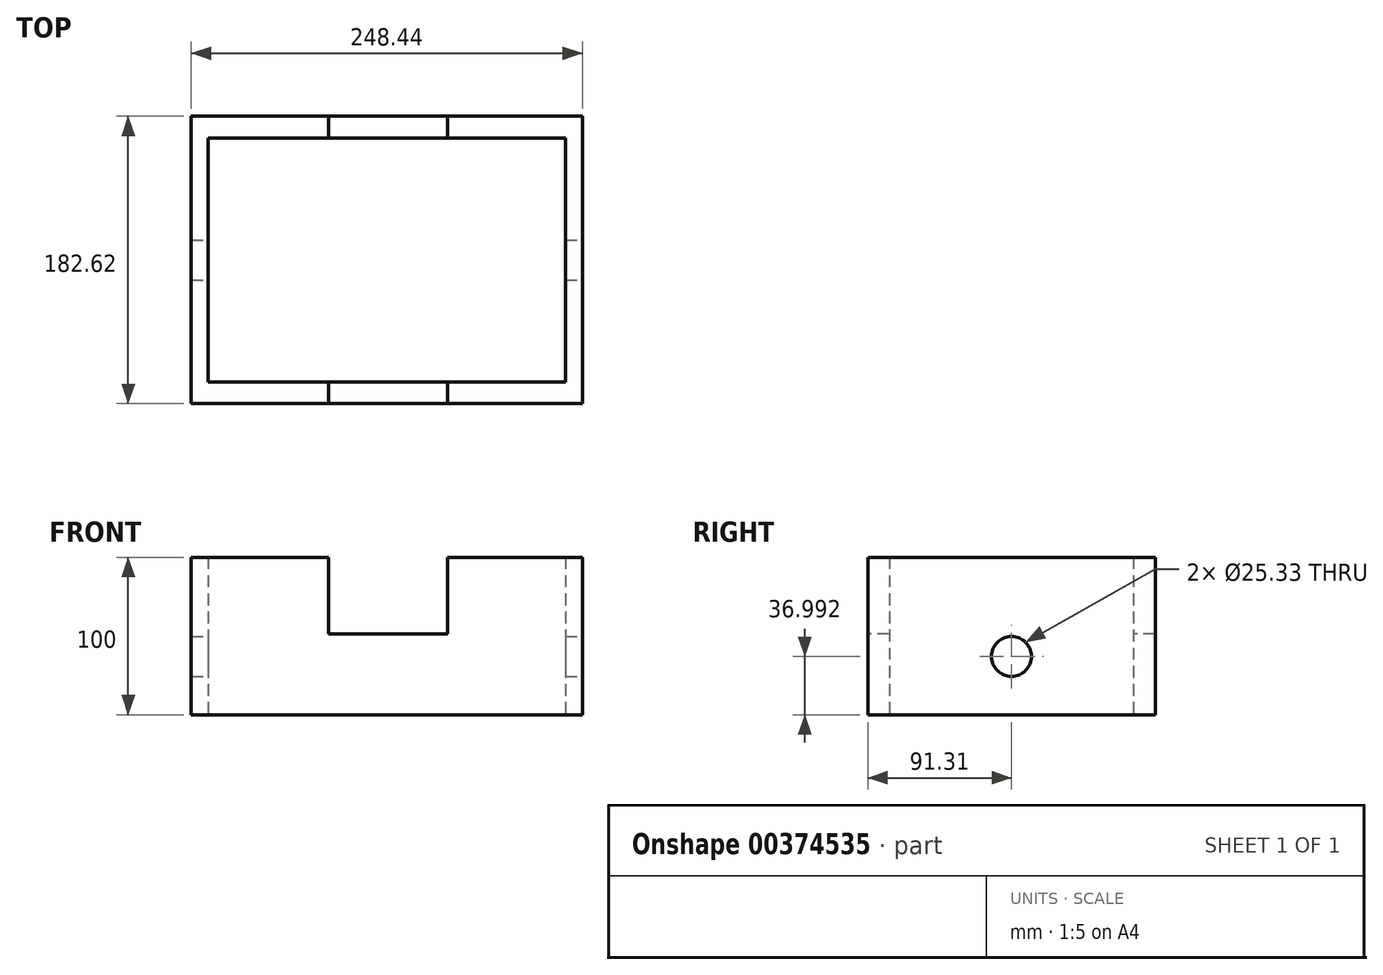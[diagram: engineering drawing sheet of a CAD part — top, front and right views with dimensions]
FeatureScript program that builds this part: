
annotation { "Feature Type Name" : "Feature", "Feature Type Description" : "" }
export const myFeature = defineFeature(function(context is Context, id is Id, definition is map)
    precondition{}
    {
        {
            var Q0;
            Q0=qCreatedBy(makeId("Top.planeOp"),FACE);
            var sketch = newSketch(context, id + "F0", { "sketchPlane" : qUnion([Q0])});
            skLineSegment(sketch, "E0.bottom", {"start": v(124.22, -91.3) * mm, "end": v(-124.22, -91.3) * mm});
            skLineSegment(sketch, "E0.top", {"start": v(124.22, 91.3) * mm, "end": v(-124.22, 91.3) * mm});
            skLineSegment(sketch, "E0.left", {"start": v(124.22, -91.3) * mm, "end": v(124.22, 91.3) * mm});
            skLineSegment(sketch, "E0.right", {"start": v(-124.22, -91.3) * mm, "end": v(-124.22, 91.3) * mm});
            skPoint(sketch, "E0.middle", {"position": v(0, 0) * mm});
            skLineSegment(sketch, "E1.bottom", {"start": v(113.4, -77.53) * mm, "end": v(-113.4, -77.53) * mm});
            skLineSegment(sketch, "E1.top", {"start": v(113.4, 77.53) * mm, "end": v(-113.4, 77.53) * mm});
            skLineSegment(sketch, "E1.left", {"start": v(113.4, -77.53) * mm, "end": v(113.4, 77.53) * mm});
            skLineSegment(sketch, "E1.right", {"start": v(-113.4, -77.53) * mm, "end": v(-113.4, 77.53) * mm});
            skSolve(sketch);
        }
        {
            var Q0;
            Q0=makeQuery(id+"F0.imprint","IMPRINT",FACE,{"disambiguationData":[TD([[makeQuery(id+"F0.imprint","IMPRINT",EDGE,{"derivedFrom":sQuery(id+"F0.wireOp",EDGE,"E0.bottom")}),-1.0]])]});
            extrude(context, id + "F1", {"entities" : qUnion([Q0]), "depth" : 100 * mm});
        }
        {
            var Q0;
            Q0=makeQuery(id+"F1.opExtrude","SWEPT_FACE",FACE,{"disambiguationData":[OSD([sQuery(id+"F0.wireOp",EDGE,"E0.bottom")])]});
            var sketch = newSketch(context, id + "F2", { "sketchPlane" : qUnion([Q0])});
            skLineSegment(sketch, "E2", {"start": v(-37.14, 100) * mm, "end": v(-37.14, 51.17) * mm});
            skLineSegment(sketch, "E3", {"start": v(-37.14, 51.17) * mm, "end": v(38.66, 51.17) * mm});
            skLineSegment(sketch, "E4", {"start": v(38.66, 51.17) * mm, "end": v(38.66, 100) * mm});
            skLineSegment(sketch, "E5", {"start": v(-37.14, 100) * mm, "end": v(38.66, 100) * mm});
            skSolve(sketch);
        }
        {
            var Q0;
            Q0 = qSketchRegion(id + "F2", true);
            extrude(context, id + "F3", {"entities" : qUnion([Q0]), "operationType" : NewBodyOperationType.REMOVE, "endBound" : BoundingType.THROUGH_ALL, "oppositeDirection" : true, "depth" : 25 * mm});
        }
        {
            var Q0;
            Q0=makeQuery(id+"F1.opExtrude","SWEPT_FACE",FACE,{"disambiguationData":[OSD([sQuery(id+"F0.wireOp",EDGE,"E0.left")])]});
            var sketch = newSketch(context, id + "F4", { "sketchPlane" : qUnion([Q0])});
            skCircle(sketch, "E6", {"center": v(0, 37) * mm, "radius": 12.67 * mm});
            skSolve(sketch);
        }
        {
            var Q0;
            Q0=makeQuery(id+"F4.imprint","IMPRINT",FACE,{"disambiguationData":[TD([[makeQuery(id+"F4.imprint","IMPRINT",EDGE,{"derivedFrom":sQuery(id+"F4.wireOp",EDGE,"E6")}),1.0]])]});
            extrude(context, id + "F5", {"entities" : qUnion([Q0]), "operationType" : NewBodyOperationType.REMOVE, "endBound" : BoundingType.THROUGH_ALL, "oppositeDirection" : true, "depth" : 25 * mm});
        }
    });
